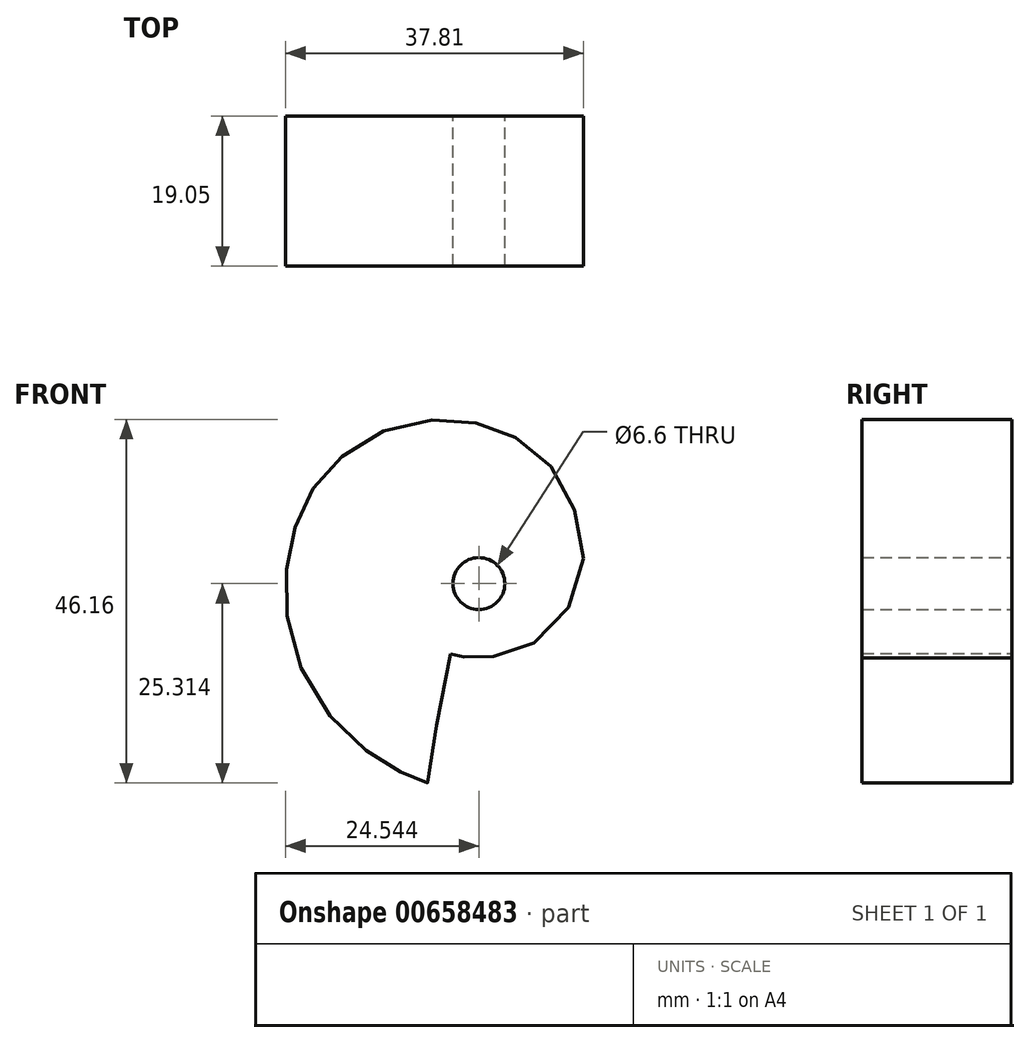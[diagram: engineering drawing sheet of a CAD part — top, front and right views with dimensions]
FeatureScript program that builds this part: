
annotation { "Feature Type Name" : "Feature", "Feature Type Description" : "" }
export const myFeature = defineFeature(function(context is Context, id is Id, definition is map)
    precondition{}
    {
        {
            var Q0;
            Q0=qCreatedBy(makeId("Front.planeOp"),FACE);
            var sketch = newSketch(context, id + "F0", { "sketchPlane" : qUnion([Q0])});
            skFitSpline(sketch, "E0", {"points": [v(1.26, -24.18) * mm, v(-1.58, -40.52) * mm, v(-1.63, -40.56) * mm, v(-3.42, -39.91) * mm, v(-7.48, -37.83) * mm, v(-13.1, -33.24) * mm, v(-18.35, -24.45) * mm, v(-19.69, -15.94) * mm, v(-18.98, -9.73) * mm, v(-16.7, -3.99) * mm, v(-12.8, 0.63) * mm, v(-6.04, 4.61) * mm, v(1.71, 5.54) * mm, v(7.19, 4.33) * mm, v(12.87, 0.92) * mm, v(17, -5.84) * mm, v(17.92, -13.8) * mm, v(13.8, -21.34) * mm, v(7.9, -24.32) * mm, v(3.84, -24.68) * mm, v(2.33, -24.46) * mm, v(1.53, -24.3) * mm, v(1.44, -24.25) * mm, v(1.26, -24.18) * mm]});
            skCircle(sketch, "E1", {"center": v(4.85, -15.26) * mm, "radius": 3.3 * mm});
            skSolve(sketch);
        }
        {
            var Q0;
            Q0 = qSketchRegion(id + "F0", true);
            extrude(context, id + "F1", {"entities" : qUnion([Q0]), "depth" : 19.05 * mm, "offsetDistance" : 25.4 * mm});
        }
    });
